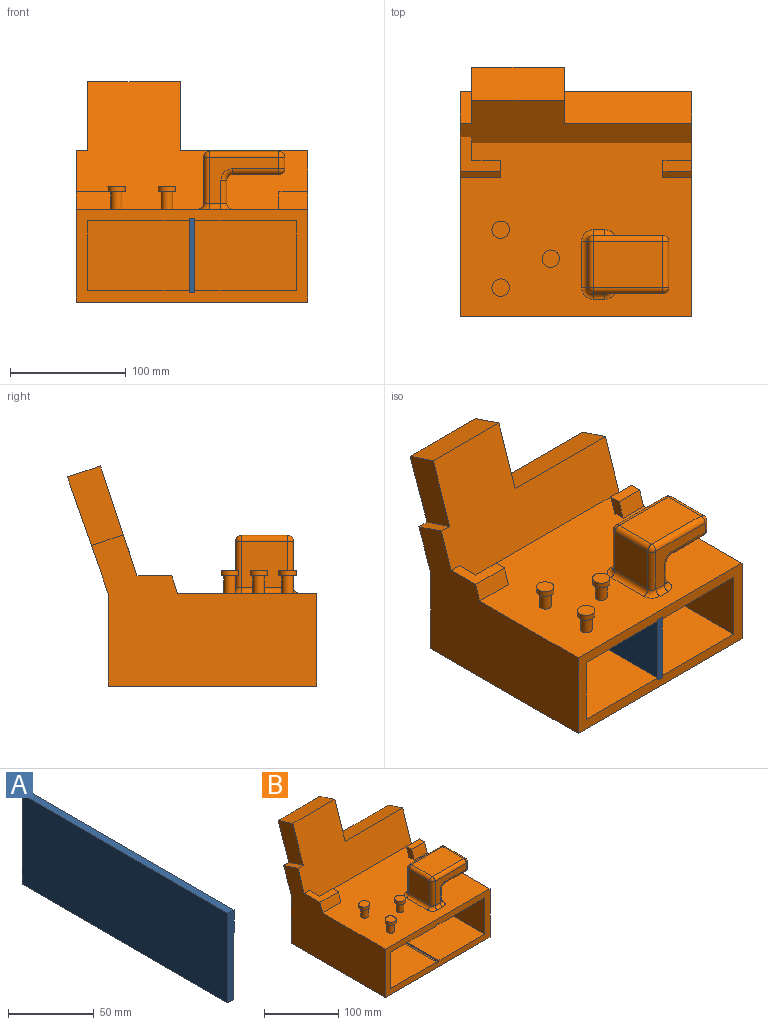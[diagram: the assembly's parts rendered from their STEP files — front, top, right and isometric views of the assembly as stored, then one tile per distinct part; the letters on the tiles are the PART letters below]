
ASSEMBLY  parts=2 mates=1
PART A: 6 faces, bbox 5x170x64 mm
  f0: plane 64x5mm, normal (0,-1,0), area 320mm2, adj f1,f3,f4,f5
  f1: plane 170x5mm, normal (0,0,-1), area 850mm2, adj f0,f2,f4,f5
  f2: plane 64x5mm, normal (0,1,0), area 320mm2, adj f1,f3,f4,f5
  f3: plane 170x5mm, normal (0,0,1), area 850mm2, adj f0,f2,f4,f5
  f4: plane 170x64mm, normal (-1,0,0), area 10880mm2, adj f0,f1,f2,f3
  f5: plane 170x64mm, normal (1,0,0), area 10880mm2, adj f0,f1,f2,f3
PART B: 85 faces, bbox 200x215.1x189.9 mm
  f0: cylinder r=5mm len=15mm, axis (0,0,-1), area 471.2mm2, adj f12,f83
  f1: cylinder r=5mm len=15mm, axis (0,0,-1), area 471.2mm2, adj f12,f80
  f2: cylinder r=5mm len=15mm, axis (0,0,-1), area 471.2mm2, adj f12,f77
  f3: plane 60x40mm, normal (0,-1,0), area 921.5mm2, adj f52,f53,f62,f63,f67,f71,f72
  f4: plane 25x10mm, normal (0,0,1), area 250mm2, adj f5,f6,f10,f39
  f5: plane 25x15mm, normal (0,0.95,-0.32), area 395.3mm2, adj f4,f10,f12,f39
  f6: plane 25x15mm, normal (0,-0.95,0.32), area 395.3mm2, adj f4,f10,f12,f39
  f7: plane 200x109.87mm, normal (0,-0.95,0.32), area 15486.3mm2, adj f8,f9,f10,f12,f29,f30,f34,f35
  f8: plane 80x28.46mm, normal (0,0.32,0.95), area 2400mm2, adj f7,f11,f34,f37
  f9: plane 194.26x130.43mm, normal (-1,0,0), area 16234.6mm2, adj f7,f11,f12,f13,f14,f15,f29,f32
  f10: plane 194.26x130.43mm, normal (1,0,0), area 15934.6mm2, adj f4,f5,f6,f7,f11,f12,f13,f14
  f11: plane 200x85.38mm, normal (0,0.94,-0.33), area 10586.3mm2, adj f8,f9,f10,f33,f34,f35,f36,f37
  f12: plane 200x150mm, normal (0,0,1), area 27250.2mm2, adj f0,f1,f2,f5,f6,f7,f9,f10
  f13: plane 200x180mm, normal (0,0,-1), area 36000mm2, adj f9,f10,f14,f15
  f14: plane 200x80mm, normal (0,1,0), area 16000mm2, adj f9,f10,f13,f33
  f15: plane 200x80mm, normal (0,-1,0), area 5180mm2, adj f9,f10,f12,f13,f16,f17,f18,f19
  f16: plane 170x60mm, normal (1,0,0), area 10200mm2, adj f15,f17,f27,f28
  f17: plane 170x87.5mm, normal (0,0,1), area 14875mm2, adj f15,f16,f18,f28
  f18: plane 170x2mm, normal (1,0,0), area 340mm2, adj f15,f17,f19,f28
  f19: plane 170x5mm, normal (0,0,1), area 850mm2, adj f15,f18,f20,f28
  f20: plane 170x2mm, normal (-1,0,0), area 340mm2, adj f15,f19,f21,f28
  f21: plane 170x87.5mm, normal (0,0,1), area 14875mm2, adj f15,f20,f22,f28
  f22: plane 170x60mm, normal (-1,0,0), area 10200mm2, adj f15,f21,f23,f28
  f23: plane 170x87.5mm, normal (0,0,-1), area 14875mm2, adj f15,f22,f24,f28
  f24: plane 170x2mm, normal (-1,0,0), area 340mm2, adj f15,f23,f25,f28
  f25: plane 170x5mm, normal (0,0,-1), area 850mm2, adj f15,f24,f26,f28
  f26: plane 170x2mm, normal (1,0,0), area 340mm2, adj f15,f25,f27,f28
  f27: plane 170x87.5mm, normal (0,0,-1), area 14875mm2, adj f15,f16,f26,f28
  f28: plane 180x64mm, normal (0,-1,0), area 10820mm2, adj f16,f17,f18,f19,f20,f21,f22,f23
  f29: plane 35x30mm, normal (0,0,1), area 550mm2, adj f7,f9,f30,f31,f32,f38
  f30: plane 25x15mm, normal (1,0,0), area 300mm2, adj f7,f12,f29,f31
  f31: plane 25x15mm, normal (0,0.95,-0.32), area 395.3mm2, adj f12,f29,f30,f38
  f32: plane 35x15mm, normal (0,-0.95,0.32), area 553.4mm2, adj f9,f12,f29,f38
  f33: plane 200x15mm, normal (0,0.95,-0.32), area 3162.3mm2, adj f9,f10,f11,f14
  f34: plane 68.58x48.27mm, normal (1,0,0), area 1846.1mm2, adj f7,f8,f11,f35
  f35: plane 110x27.45mm, normal (0,0.32,0.95), area 3182.8mm2, adj f7,f10,f11,f34
  f36: plane 27.45x10mm, normal (0,0.32,0.95), area 289.3mm2, adj f7,f9,f11,f37
  f37: plane 68.58x48.27mm, normal (-1,0,0), area 1846.1mm2, adj f7,f8,f11,f36
  f38: plane 15x15mm, normal (1,0,0), area 150mm2, adj f12,f29,f31,f32
  f39: plane 15x15mm, normal (-1,0,0), area 150mm2, adj f4,f5,f6,f12
  f40: plane 60x40mm, normal (0,1,0), area 921.5mm2, adj f49,f50,f59,f60,f66,f69,f70
  f41: plane 40x40mm, normal (-1,0,0), area 1600mm2, adj f46,f49,f53,f54
  f42: plane 40x10mm, normal (1,0,0), area 400mm2, adj f64,f69,f72,f75
  f43: plane 60x40mm, normal (0,0,1), area 2400mm2, adj f54,f59,f63,f64
  f44: plane 40x40mm, normal (0,0,-1), area 1600mm2, adj f61,f70,f71,f75
  f45: plane 40x20mm, normal (1,0,0), area 800mm2, adj f51,f60,f61,f62
  f46: cylinder r=5mm len=40mm, axis (0,1,0), area 314.2mm2, adj f12,f41,f47,f48
  f47: torus R=10mm, axis (0,0,-1), area 84.1mm2, adj f12,f46,f49,f50
  f48: torus R=10mm, axis (0,0,-1), area 84.1mm2, adj f12,f46,f52,f53
  f49: cylinder r=5mm len=40mm, axis (0,0,1), area 314.2mm2, adj f40,f41,f47,f55
  f50: cylinder r=5mm len=10mm, axis (1,0,0), area 78.5mm2, adj f12,f40,f47,f56
  f51: cylinder r=5mm len=40mm, axis (0,-1,0), area 314.2mm2, adj f12,f45,f56,f57
  f52: cylinder r=5mm len=10mm, axis (-1,0,0), area 78.5mm2, adj f3,f12,f48,f57
  f53: cylinder r=5mm len=40mm, axis (0,0,-1), area 314.2mm2, adj f3,f41,f48,f58
  f54: cylinder r=5mm len=40mm, axis (0,1,0), area 314.2mm2, adj f41,f43,f55,f58
  f55: sphere r=5mm, area 39.3mm2, adj f49,f54,f59
  f56: torus R=10mm, axis (0,0,-1), area 84.1mm2, adj f12,f50,f51,f60
  f57: torus R=10mm, axis (0,0,-1), area 84.1mm2, adj f12,f51,f52,f62
  f58: sphere r=5mm, area 39.3mm2, adj f53,f54,f63
  f59: cylinder r=5mm len=60mm, axis (1,0,0), area 471.2mm2, adj f40,f43,f55,f65
  f60: cylinder r=5mm len=20mm, axis (0,0,1), area 157.1mm2, adj f40,f45,f56,f66
  f61: cylinder r=5mm len=40mm, axis (0,-1,0), area 314.2mm2, adj f44,f45,f66,f67
  f62: cylinder r=5mm len=20mm, axis (0,0,-1), area 157.1mm2, adj f3,f45,f57,f67
  f63: cylinder r=5mm len=60mm, axis (-1,0,0), area 471.2mm2, adj f3,f43,f58,f68
  f64: cylinder r=5mm len=40mm, axis (0,-1,0), area 314.2mm2, adj f42,f43,f65,f68
  f65: sphere r=5mm, area 39.3mm2, adj f59,f64,f69
  f66: torus R=10mm, axis (0,1,0), area 84.1mm2, adj f40,f60,f61,f70
  f67: torus R=10mm, axis (0,1,0), area 84.1mm2, adj f3,f61,f62,f71
  f68: sphere r=5mm, area 39.3mm2, adj f63,f64,f72
  f69: cylinder r=5mm len=10mm, axis (0,0,-1), area 78.5mm2, adj f40,f42,f65,f73
  f70: cylinder r=5mm len=40mm, axis (1,0,0), area 314.2mm2, adj f40,f44,f66,f73
  f71: cylinder r=5mm len=40mm, axis (-1,0,0), area 314.2mm2, adj f3,f44,f67,f74
  f72: cylinder r=5mm len=10mm, axis (0,0,1), area 78.5mm2, adj f3,f42,f68,f74
  f73: sphere r=5mm, area 39.3mm2, adj f69,f70,f75
  f74: sphere r=5mm, area 39.3mm2, adj f71,f72,f75
  f75: cylinder r=5mm len=40mm, axis (0,1,0), area 314.2mm2, adj f42,f44,f73,f74
  f76: cylinder r=7.5mm len=15mm, axis (0,0,1), area 235.6mm2, adj f77,f78
  f77: plane 15x15mm, normal (0,0,-1), area 98.2mm2, adj f2,f76
  f78: plane 15x15mm, normal (0,0,1), area 176.7mm2, adj f76
  f79: cylinder r=7.5mm len=15mm, axis (0,0,1), area 235.6mm2, adj f80,f81
  f80: plane 15x15mm, normal (0,0,-1), area 98.2mm2, adj f1,f79
  f81: plane 15x15mm, normal (0,0,1), area 176.7mm2, adj f79
  f82: cylinder r=7.5mm len=15mm, axis (0,0,1), area 235.6mm2, adj f83,f84
  f83: plane 15x15mm, normal (0,0,-1), area 98.2mm2, adj f0,f82
  f84: plane 15x15mm, normal (0,0,1), area 176.7mm2, adj f82
PLACE A t=(-17.39,-81.7,-26.79)mm
PLACE B t=(-119.89,-81.7,-34.79)mm
MATE fastened A.f2 <-> B.f28  axis (0,1,0) through (-19.89,88.3,5.21)mm
